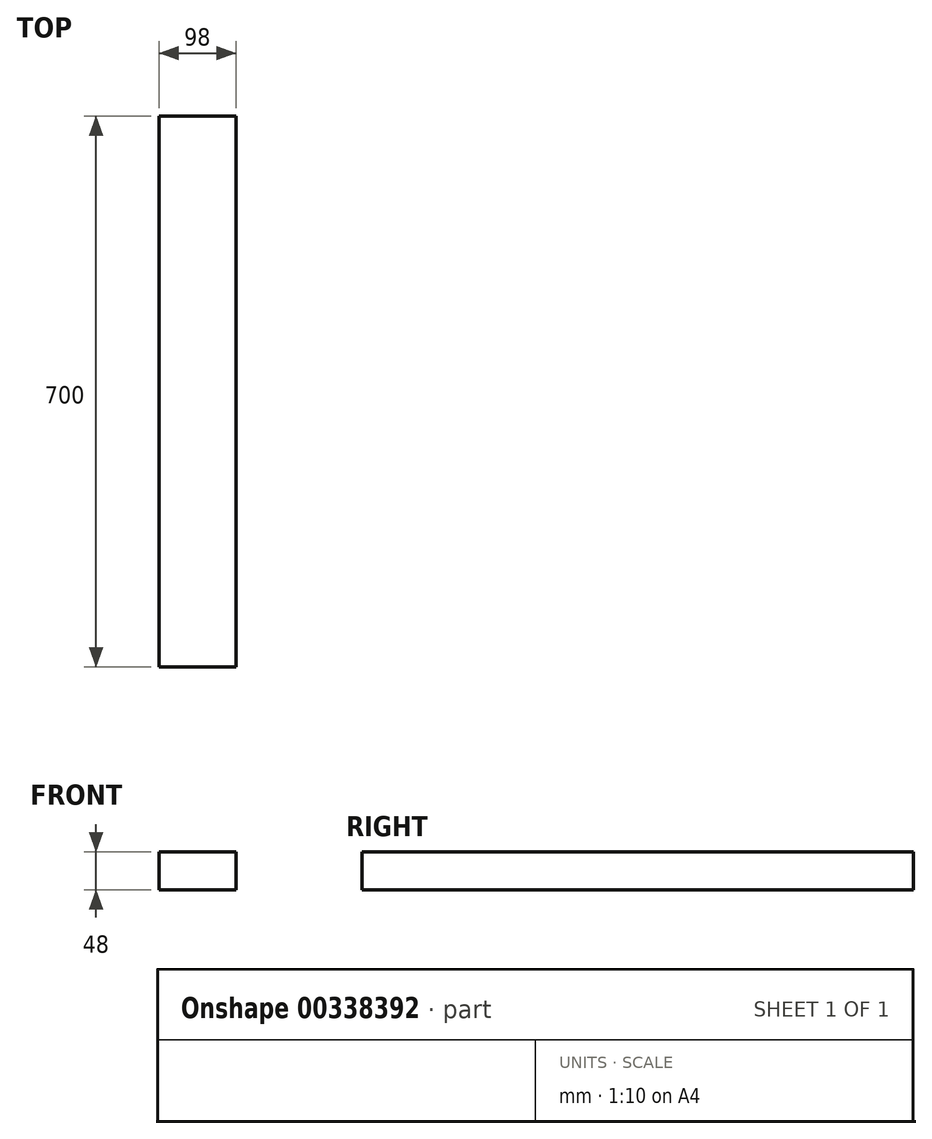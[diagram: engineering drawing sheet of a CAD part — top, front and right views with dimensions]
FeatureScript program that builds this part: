
annotation { "Feature Type Name" : "Feature", "Feature Type Description" : "" }
export const myFeature = defineFeature(function(context is Context, id is Id, definition is map)
    precondition{}
    {
        {
            var Q0;
            Q0=qCreatedBy(makeId("Front.planeOp"),FACE);
            var sketch = newSketch(context, id + "F0", { "sketchPlane" : qUnion([Q0])});
            skLineSegment(sketch, "E0.bottom", {"start": v(-49, -24) * mm, "end": v(49, -24) * mm});
            skLineSegment(sketch, "E0.top", {"start": v(-49, 24) * mm, "end": v(49, 24) * mm});
            skLineSegment(sketch, "E0.left", {"start": v(-49, -24) * mm, "end": v(-49, 24) * mm});
            skLineSegment(sketch, "E0.right", {"start": v(49, -24) * mm, "end": v(49, 24) * mm});
            skPoint(sketch, "E0.middle", {"position": v(0, 0) * mm});
            skSolve(sketch);
        }
        {
            var Q0;
            Q0=makeQuery(id+"F0.imprint","IMPRINT",FACE,{"disambiguationData":[TD([[makeQuery(id+"F0.imprint","IMPRINT",EDGE,{"derivedFrom":sQuery(id+"F0.wireOp",EDGE,"E0.bottom")}),1.0]])]});
            extrude(context, id + "F1", {"entities" : qUnion([Q0]), "offsetDistance" : 25 * mm, "depth" : 700 * mm});
        }
    });
